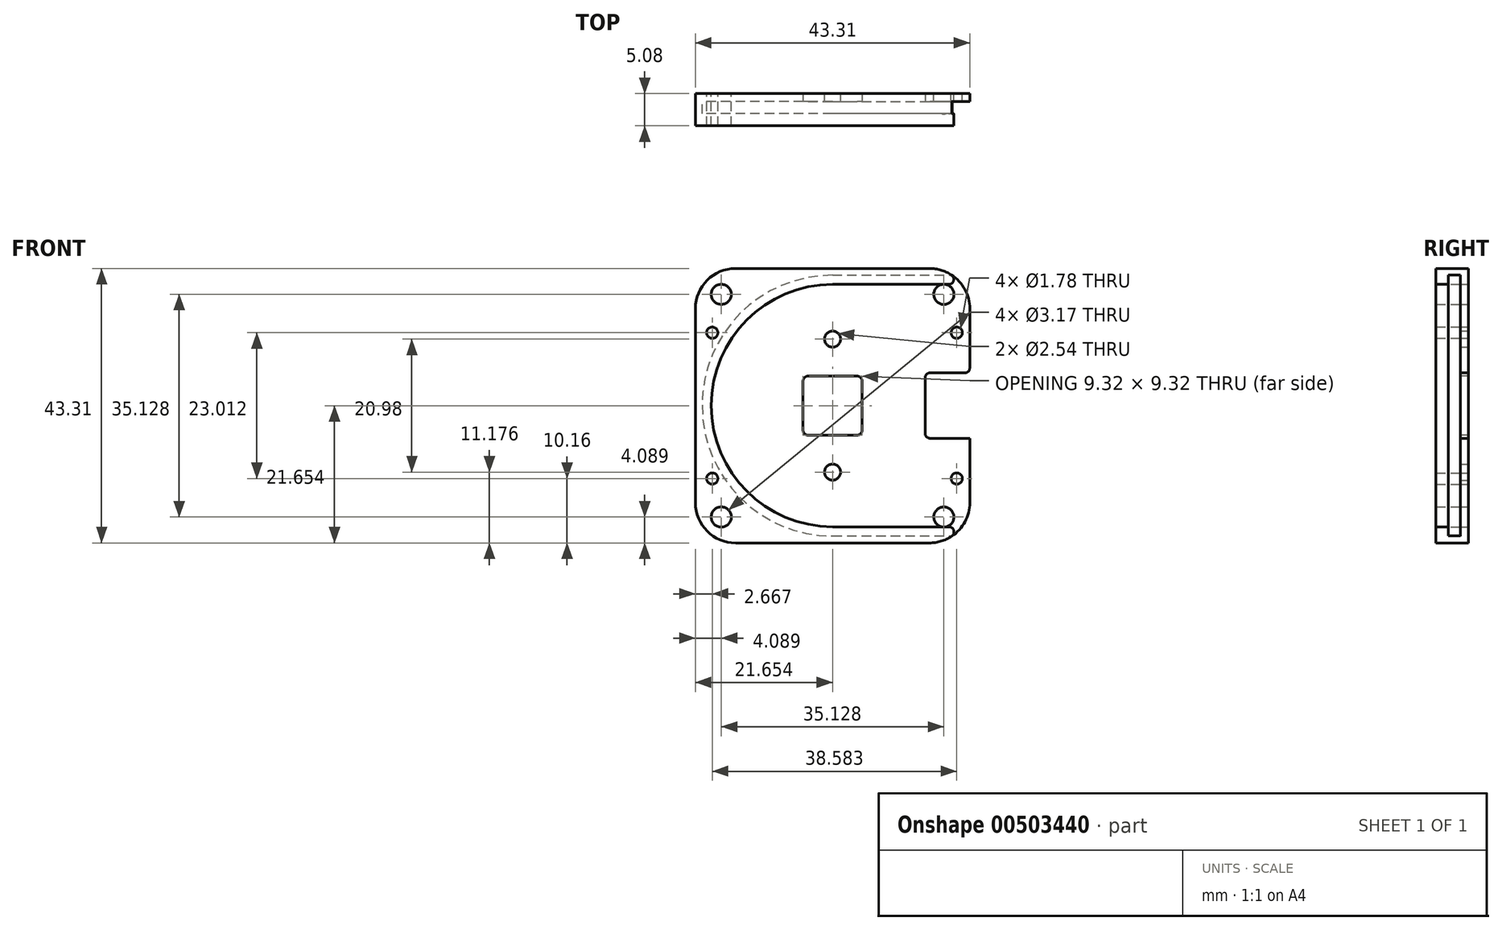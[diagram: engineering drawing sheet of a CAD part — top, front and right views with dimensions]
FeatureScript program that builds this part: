
annotation { "Feature Type Name" : "Feature", "Feature Type Description" : "" }
export const myFeature = defineFeature(function(context is Context, id is Id, definition is map)
    precondition{}
    {
        {
            var Q0;
            Q0=qCreatedBy(makeId("Front.planeOp"),FACE);
            var sketch = newSketch(context, id + "F0", { "sketchPlane" : qUnion([Q0])});
            skLineSegment(sketch, "E0.bottom", {"start": v(0, 0) * mm, "end": v(43.3, 0) * mm});
            skLineSegment(sketch, "E0.top", {"start": v(0, 43.3) * mm, "end": v(43.3, 43.3) * mm});
            skLineSegment(sketch, "E0.left", {"start": v(0, 0) * mm, "end": v(0, 43.3) * mm});
            skLineSegment(sketch, "E0.right", {"start": v(43.3, 0) * mm, "end": v(43.3, 43.3) * mm});
            skSolve(sketch);
        }
        {
            var Q0;
            Q0=makeQuery(id+"F0.imprint","IMPRINT",FACE,{"disambiguationData":[TD([[makeQuery(id+"F0.imprint","IMPRINT",EDGE,{"derivedFrom":sQuery(id+"F0.wireOp",EDGE,"E0.bottom")}),1.0]])]});
            extrude(context, id + "F1", {"entities" : qUnion([Q0]), "depth" : 1.27 * mm});
        }
        {
            var Q0;
            Q0=qCreatedBy(makeId("Front.planeOp"),FACE);
            var sketch = newSketch(context, id + "F2", { "sketchPlane" : qUnion([Q0])});
            skLineSegment(sketch, "E1", {"start": v(0, 43.3) * mm, "end": v(43.3, 43.3) * mm});
            skLineSegment(sketch, "E2", {"start": v(43.3, 43.3) * mm, "end": v(43.3, 42.24) * mm});
            skLineSegment(sketch, "E3", {"start": v(43.3, 42.24) * mm, "end": v(21.64, 42.24) * mm});
            skLineSegment(sketch, "E4", {"start": v(0, 0) * mm, "end": v(43.3, 0) * mm});
            skLineSegment(sketch, "E5", {"start": v(43.3, 0) * mm, "end": v(43.3, 1.1) * mm});
            skLineSegment(sketch, "E6", {"start": v(43.3, 1.1) * mm, "end": v(21.64, 1.1) * mm});
            skArc(sketch, "E7", {"start": v(21.64, 42.24) * mm, "mid": v(1.07, 21.67) * mm, "end": v(21.64, 1.1) * mm});
            skLineSegment(sketch, "E8", {"start": v(0, 43.3) * mm, "end": v(0, 0) * mm});
            skSolve(sketch);
        }
        {
            var Q0;
            Q0 = qSketchRegion(id + "F2", true);
            extrude(context, id + "F3", {"entities" : qUnion([Q0]), "operationType" : NewBodyOperationType.ADD, "depth" : 3.17 * mm});
        }
        {
            var Q0;
            Q0=makeQuery(id+"F3.opExtrude","CAP_FACE",FACE,{"disambiguationData":[OSD([sQuery(id+"F2.wireOp",EDGE,"E1"),sQuery(id+"F2.wireOp",EDGE,"E2"),sQuery(id+"F2.wireOp",EDGE,"E3"),sQuery(id+"F2.wireOp",EDGE,"E4"),sQuery(id+"F2.wireOp",EDGE,"E5"),sQuery(id+"F2.wireOp",EDGE,"E6"),sQuery(id+"F2.wireOp",EDGE,"E7"),sQuery(id+"F2.wireOp",EDGE,"E8")])],"isStart":false});
            var sketch = newSketch(context, id + "F4", { "sketchPlane" : qUnion([Q0])});
            skLineSegment(sketch, "E9", {"start": v(0, 43.3) * mm, "end": v(43.3, 43.3) * mm});
            skLineSegment(sketch, "E10", {"start": v(0, 43.3) * mm, "end": v(0, 0) * mm});
            skLineSegment(sketch, "E11", {"start": v(0, 0) * mm, "end": v(43.3, 0) * mm});
            skLineSegment(sketch, "E12", {"start": v(43.3, 0) * mm, "end": v(43.3, 2.54) * mm});
            skLineSegment(sketch, "E13", {"start": v(43.3, 2.54) * mm, "end": v(21.64, 2.54) * mm});
            skLineSegment(sketch, "E14", {"start": v(43.3, 43.3) * mm, "end": v(43.3, 40.8) * mm});
            skLineSegment(sketch, "E15", {"start": v(43.3, 40.8) * mm, "end": v(21.64, 40.8) * mm});
            skArc(sketch, "E16", {"start": v(21.64, 40.8) * mm, "mid": v(2.51, 21.67) * mm, "end": v(21.64, 2.54) * mm});
            skSolve(sketch);
        }
        {
            var Q0;
            Q0 = qSketchRegion(id + "F4", true);
            extrude(context, id + "F5", {"entities" : qUnion([Q0]), "operationType" : NewBodyOperationType.ADD, "depth" : 1.9 * mm, "offsetDistance" : 25.4 * mm});
        }
        {
            var Q0;
            Q0=makeQuery(id+"F1.opExtrude","CAP_FACE",FACE,{"disambiguationData":[OSD([sQuery(id+"F0.wireOp",EDGE,"E0.bottom"),sQuery(id+"F0.wireOp",EDGE,"E0.top"),sQuery(id+"F0.wireOp",EDGE,"E0.left"),sQuery(id+"F0.wireOp",EDGE,"E0.right")])],"isStart":true});
            var sketch = newSketch(context, id + "F6", { "sketchPlane" : qUnion([Q0])});
            skCircle(sketch, "E17", {"center": v(-41.25, 33.17) * mm, "radius": 0.89 * mm});
            skCircle(sketch, "E18", {"center": v(-2.67, 33.17) * mm, "radius": 0.89 * mm});
            skCircle(sketch, "E19", {"center": v(-41.25, 10.16) * mm, "radius": 0.89 * mm});
            skCircle(sketch, "E20", {"center": v(-2.67, 10.16) * mm, "radius": 0.89 * mm});
            skSolve(sketch);
        }
        {
            var Q0;
            Q0 = qSketchRegion(id + "F6", true);
            extrude(context, id + "F7", {"entities" : qUnion([Q0]), "operationType" : NewBodyOperationType.REMOVE, "endBound" : BoundingType.UP_TO_NEXT, "oppositeDirection" : true, "depth" : 25.4 * mm});
        }
        {
            var Q0;
            Q0=makeQuery(id+"F1.opExtrude","CAP_FACE",FACE,{"disambiguationData":[OSD([sQuery(id+"F0.wireOp",EDGE,"E0.bottom"),sQuery(id+"F0.wireOp",EDGE,"E0.top"),sQuery(id+"F0.wireOp",EDGE,"E0.left"),sQuery(id+"F0.wireOp",EDGE,"E0.right")])],"isStart":false});
            var sketch = newSketch(context, id + "F8", { "sketchPlane" : qUnion([Q0])});
            skLineSegment(sketch, "E21.bottom", {"start": v(17, 26.31) * mm, "end": v(26.31, 26.31) * mm});
            skLineSegment(sketch, "E21.top", {"start": v(17, 17) * mm, "end": v(26.31, 17) * mm});
            skLineSegment(sketch, "E21.left", {"start": v(17, 26.31) * mm, "end": v(17, 17) * mm});
            skLineSegment(sketch, "E21.right", {"start": v(26.31, 26.31) * mm, "end": v(26.31, 17) * mm});
            skLineSegment(sketch, "E22", {"start": v(43.3, 26.82) * mm, "end": v(36.25, 26.82) * mm});
            skLineSegment(sketch, "E23", {"start": v(36.25, 26.82) * mm, "end": v(36.25, 16.51) * mm});
            skLineSegment(sketch, "E24", {"start": v(36.25, 16.51) * mm, "end": v(43.3, 16.51) * mm});
            skLineSegment(sketch, "E25", {"start": v(43.3, 16.51) * mm, "end": v(43.3, 26.82) * mm});
            skSolve(sketch);
        }
        {
            var Q0;
            Q0=makeQuery(id+"F1.opExtrude","CAP_FACE",FACE,{"disambiguationData":[OSD([sQuery(id+"F0.wireOp",EDGE,"E0.bottom"),sQuery(id+"F0.wireOp",EDGE,"E0.top"),sQuery(id+"F0.wireOp",EDGE,"E0.left"),sQuery(id+"F0.wireOp",EDGE,"E0.right")])],"isStart":true});
            var sketch = newSketch(context, id + "F9", { "sketchPlane" : qUnion([Q0])});
            skPoint(sketch, "E26", {"position": v(-4.09, 39.22) * mm});
            skPoint(sketch, "E27", {"position": v(-39.22, 39.22) * mm});
            skPoint(sketch, "E28", {"position": v(-39.22, 4.09) * mm});
            skPoint(sketch, "E29", {"position": v(-4.09, 4.09) * mm});
            skSolve(sketch);
        }
        {
            var Q0;
            Q0 = qSketchRegion(id + "F8", true);
            extrude(context, id + "F10", {"entities" : qUnion([Q0]), "operationType" : NewBodyOperationType.REMOVE, "endBound" : BoundingType.UP_TO_NEXT, "oppositeDirection" : true, "depth" : 25.4 * mm});
        }
        {
            var Q0;
            Q0=sQuery(id+"F9.wireOp",VERTEX,"E26");
            var Q1;
            Q1=sQuery(id+"F9.wireOp",VERTEX,"E29");
            var Q2;
            Q2=makeQuery(id+"F1.opExtrude","SWEPT_BODY",BODY,{"disambiguationData":[OSD([sQuery(id+"F0.wireOp",EDGE,"E0.bottom"),sQuery(id+"F0.wireOp",EDGE,"E0.top"),sQuery(id+"F0.wireOp",EDGE,"E0.left"),sQuery(id+"F0.wireOp",EDGE,"E0.right")])]});
            hole(context, id + "F11", {"style" : HoleStyle.SIMPLE, "endStyle" : HoleEndStyle.THROUGH, "holeDiameter" : 3.17 * mm, "isTappedThrough" : true, "tappedDepth" : 12.7 * mm, "tapClearance" : 3, "locations" : qUnion([Q0, Q1]), "scope" : qUnion([Q2])});
        }
        {
            var Q0;
            Q0=makeQuery(id+"F1.opExtrude","CAP_FACE",FACE,{"disambiguationData":[OSD([sQuery(id+"F0.wireOp",EDGE,"E0.bottom"),sQuery(id+"F0.wireOp",EDGE,"E0.top"),sQuery(id+"F0.wireOp",EDGE,"E0.left"),sQuery(id+"F0.wireOp",EDGE,"E0.right")])],"isStart":true});
            var sketch = newSketch(context, id + "F12", { "sketchPlane" : qUnion([Q0])});
            skLineSegment(sketch, "E30", {"start": v(-39.22, 39.22) * mm, "end": v(-4.09, 39.22) * mm, "construction": true});
            skLineSegment(sketch, "E31", {"start": v(-4.09, 39.22) * mm, "end": v(-4.09, 4.09) * mm, "construction": true});
            skLineSegment(sketch, "E32", {"start": v(-4.09, 4.09) * mm, "end": v(-39.22, 4.09) * mm, "construction": true});
            skLineSegment(sketch, "E33", {"start": v(-39.22, 4.09) * mm, "end": v(-39.22, 39.22) * mm, "construction": true});
            skSolve(sketch);
        }
        {
            var Q0;
            Q0=makeQuery(id+"F1.opExtrude","CAP_FACE",FACE,{"disambiguationData":[OSD([sQuery(id+"F0.wireOp",EDGE,"E0.bottom"),sQuery(id+"F0.wireOp",EDGE,"E0.top"),sQuery(id+"F0.wireOp",EDGE,"E0.left"),sQuery(id+"F0.wireOp",EDGE,"E0.right")])],"isStart":true});
            var sketch = newSketch(context, id + "F13", { "sketchPlane" : qUnion([Q0])});
            skLineSegment(sketch, "E34", {"start": v(-21.65, 32.16) * mm, "end": v(-21.65, 11.18) * mm});
            skPoint(sketch, "E34.startSnap0", {"position": v(-21.65, 26.31) * mm});
            skPoint(sketch, "E34.endSnap0", {"position": v(-21.65, 26.31) * mm});
            skSolve(sketch);
        }
        {
            var Q0;
            Q0=sQuery(id+"F13.wireOp",VERTEX,"E34.start");
            var Q1;
            Q1=sQuery(id+"F13.wireOp",VERTEX,"E34.end");
            var Q2;
            Q2=makeQuery(id+"F1.opExtrude","SWEPT_BODY",BODY,{"disambiguationData":[OSD([sQuery(id+"F0.wireOp",EDGE,"E0.bottom"),sQuery(id+"F0.wireOp",EDGE,"E0.top"),sQuery(id+"F0.wireOp",EDGE,"E0.left"),sQuery(id+"F0.wireOp",EDGE,"E0.right")])]});
            hole(context, id + "F14", {"style" : HoleStyle.SIMPLE, "endStyle" : HoleEndStyle.THROUGH, "holeDiameter" : 2.54 * mm, "isTappedThrough" : true, "tappedDepth" : 12.7 * mm, "tapClearance" : 3, "locations" : qUnion([Q0, Q1]), "scope" : qUnion([Q2])});
        }
        {
            var Q0;
            Q0=makeQuery(id+"F5.boolean.opBoolean","MERGE",EDGE,{"derivedFrom":[makeQuery(id+"F3.boolean.opBoolean","MERGE",EDGE,{"derivedFrom":[makeQuery(id+"F1.opExtrude","SWEPT_EDGE",EDGE,{"disambiguationData":[OSD([sQuery(id+"F0.wireOp",EDGE,"E0.top"),sQuery(id+"F0.wireOp",EDGE,"E0.left")])]}),makeQuery(id+"F3.opExtrude","SWEPT_EDGE",EDGE,{"disambiguationData":[OSD([sQuery(id+"F2.wireOp",EDGE,"E1"),sQuery(id+"F2.wireOp",EDGE,"E8")])]})]}),makeQuery(id+"F5.opExtrude","SWEPT_EDGE",EDGE,{"disambiguationData":[OSD([sQuery(id+"F4.wireOp",EDGE,"E9"),sQuery(id+"F4.wireOp",EDGE,"E10")])]})]});
            var Q1;
            Q1=makeQuery(id+"F5.boolean.opBoolean","MERGE",EDGE,{"derivedFrom":[makeQuery(id+"F3.boolean.opBoolean","MERGE",EDGE,{"derivedFrom":[makeQuery(id+"F1.opExtrude","SWEPT_EDGE",EDGE,{"disambiguationData":[OSD([sQuery(id+"F0.wireOp",EDGE,"E0.top"),sQuery(id+"F0.wireOp",EDGE,"E0.right")])]}),makeQuery(id+"F3.opExtrude","SWEPT_EDGE",EDGE,{"disambiguationData":[OSD([sQuery(id+"F2.wireOp",EDGE,"E1"),sQuery(id+"F2.wireOp",EDGE,"E2")])]})]}),makeQuery(id+"F5.opExtrude","SWEPT_EDGE",EDGE,{"disambiguationData":[OSD([sQuery(id+"F4.wireOp",EDGE,"E9"),sQuery(id+"F4.wireOp",EDGE,"E14")])]})]});
            var Q2;
            Q2=makeQuery(id+"F5.boolean.opBoolean","MERGE",EDGE,{"derivedFrom":[makeQuery(id+"F3.boolean.opBoolean","MERGE",EDGE,{"derivedFrom":[makeQuery(id+"F1.opExtrude","SWEPT_EDGE",EDGE,{"disambiguationData":[OSD([sQuery(id+"F0.wireOp",EDGE,"E0.bottom"),sQuery(id+"F0.wireOp",EDGE,"E0.right")])]}),makeQuery(id+"F3.opExtrude","SWEPT_EDGE",EDGE,{"disambiguationData":[OSD([sQuery(id+"F2.wireOp",EDGE,"E4"),sQuery(id+"F2.wireOp",EDGE,"E5")])]})]}),makeQuery(id+"F5.opExtrude","SWEPT_EDGE",EDGE,{"disambiguationData":[OSD([sQuery(id+"F4.wireOp",EDGE,"E11"),sQuery(id+"F4.wireOp",EDGE,"E12")])]})]});
            var Q3;
            Q3=makeQuery(id+"F5.boolean.opBoolean","MERGE",EDGE,{"derivedFrom":[makeQuery(id+"F3.boolean.opBoolean","MERGE",EDGE,{"derivedFrom":[makeQuery(id+"F1.opExtrude","SWEPT_EDGE",EDGE,{"disambiguationData":[OSD([sQuery(id+"F0.wireOp",EDGE,"E0.bottom"),sQuery(id+"F0.wireOp",EDGE,"E0.left")])]}),makeQuery(id+"F3.opExtrude","SWEPT_EDGE",EDGE,{"disambiguationData":[OSD([sQuery(id+"F2.wireOp",EDGE,"E4"),sQuery(id+"F2.wireOp",EDGE,"E8")])]})]}),makeQuery(id+"F5.opExtrude","SWEPT_EDGE",EDGE,{"disambiguationData":[OSD([sQuery(id+"F4.wireOp",EDGE,"E10"),sQuery(id+"F4.wireOp",EDGE,"E11")])]})]});
            fillet(context, id + "F15", {"entities" : qUnion([Q0, Q1, Q2, Q3]), "radius" : 6.35 * mm, "tangentPropagation" : true, "allowEdgeOverflow" : false});
        }
        {
            var Q0;
            {var subQ1=sQuery(id+"F4.wireOp",EDGE,"E15");var subQ2=sQuery(id+"F4.wireOp",EDGE,"E14");var subQ7=sQuery(id+"F4.wireOp",EDGE,"E9");var subQ8=sQuery(id+"F2.wireOp",EDGE,"E2");var subQ9=sQuery(id+"F0.wireOp",EDGE,"E0.right");Q0=makeQuery(id+"F15.opFillet","BLEND_EDGE",EDGE,{"blendedFrom":[makeQuery(id+"F5.boolean.opBoolean","MERGE",EDGE,{"derivedFrom":[makeQuery(id+"F3.boolean.opBoolean","MERGE",EDGE,{"derivedFrom":[makeQuery(id+"F1.opExtrude","SWEPT_EDGE",EDGE,{"disambiguationData":[OSD([sQuery(id+"F0.wireOp",EDGE,"E0.top"),subQ9])]}),makeQuery(id+"F3.opExtrude","SWEPT_EDGE",EDGE,{"disambiguationData":[OSD([sQuery(id+"F2.wireOp",EDGE,"E1"),subQ8])]})]}),makeQuery(id+"F5.opExtrude","SWEPT_EDGE",EDGE,{"disambiguationData":[OSD([subQ7,subQ2])]})]}),makeQuery(id+"FAVqUnOOAbN4NIG_1.hole-0.boolean.opBoolean","SPLIT",FACE,{"disambiguationData":[TD([makeQuery(id+"F1.opExtrude","SWEPT_FACE",FACE,{"disambiguationData":[OSD([subQ9])]})])],"derivedFrom":makeQuery(id+"F5.opExtrude","SWEPT_FACE",FACE,{"disambiguationData":[OSD([subQ1])]})})],"blendedInto":[makeQuery(id+"FAVqUnOOAbN4NIG_1.hole-0.boolean.opBoolean","SPLIT",FACE,{"disambiguationData":[TD([makeQuery(id+"F1.opExtrude","SWEPT_FACE",FACE,{"disambiguationData":[OSD([subQ9])]})])],"derivedFrom":makeQuery(id+"F5.opExtrude","SWEPT_FACE",FACE,{"disambiguationData":[OSD([subQ1])]})})]});}
            var Q1;
            {var subQ3=sQuery(id+"F4.wireOp",EDGE,"E13");var subQ4=sQuery(id+"F4.wireOp",EDGE,"E12");var subQ5=sQuery(id+"F4.wireOp",EDGE,"E11");var subQ8=sQuery(id+"F2.wireOp",EDGE,"E5");var subQ9=sQuery(id+"F0.wireOp",EDGE,"E0.right");Q1=makeQuery(id+"F15.opFillet","BLEND_EDGE",EDGE,{"blendedFrom":[makeQuery(id+"F5.boolean.opBoolean","MERGE",EDGE,{"derivedFrom":[makeQuery(id+"F3.boolean.opBoolean","MERGE",EDGE,{"derivedFrom":[makeQuery(id+"F1.opExtrude","SWEPT_EDGE",EDGE,{"disambiguationData":[OSD([sQuery(id+"F0.wireOp",EDGE,"E0.bottom"),subQ9])]}),makeQuery(id+"F3.opExtrude","SWEPT_EDGE",EDGE,{"disambiguationData":[OSD([sQuery(id+"F2.wireOp",EDGE,"E4"),subQ8])]})]}),makeQuery(id+"F5.opExtrude","SWEPT_EDGE",EDGE,{"disambiguationData":[OSD([subQ5,subQ4])]})]}),makeQuery(id+"FAVqUnOOAbN4NIG_1.hole-3.boolean.opBoolean","SPLIT",FACE,{"disambiguationData":[TD([makeQuery(id+"F1.opExtrude","SWEPT_FACE",FACE,{"disambiguationData":[OSD([subQ9])]})])],"derivedFrom":makeQuery(id+"F5.opExtrude","SWEPT_FACE",FACE,{"disambiguationData":[OSD([subQ3])]})})],"blendedInto":[makeQuery(id+"FAVqUnOOAbN4NIG_1.hole-3.boolean.opBoolean","SPLIT",FACE,{"disambiguationData":[TD([makeQuery(id+"F1.opExtrude","SWEPT_FACE",FACE,{"disambiguationData":[OSD([subQ9])]})])],"derivedFrom":makeQuery(id+"F5.opExtrude","SWEPT_FACE",FACE,{"disambiguationData":[OSD([subQ3])]})})]});}
            fillet(context, id + "F16", {"entities" : qUnion([Q0, Q1]), "radius" : 0.81 * mm, "tangentPropagation" : true, "allowEdgeOverflow" : false});
        }
        {
            var Q0;
            Q0=makeQuery(id+"F10.boolean.opBoolean","COPY",EDGE,{"derivedFrom":makeQuery(id+"F10.opExtrude","SWEPT_EDGE",EDGE,{"disambiguationData":[OSD([sQuery(id+"F0.wireOp",EDGE,"E0.right"),sQuery(id+"F8.wireOp",EDGE,"E22"),sQuery(id+"F8.wireOp",EDGE,"E25")])]})});
            var Q1;
            Q1=makeQuery(id+"F10.boolean.opBoolean","COPY",EDGE,{"derivedFrom":makeQuery(id+"F10.opExtrude","SWEPT_EDGE",EDGE,{"disambiguationData":[OSD([sQuery(id+"F8.wireOp",EDGE,"E22"),sQuery(id+"F8.wireOp",EDGE,"E23")])]})});
            var Q2;
            Q2=makeQuery(id+"F10.boolean.opBoolean","COPY",EDGE,{"derivedFrom":makeQuery(id+"F10.opExtrude","SWEPT_EDGE",EDGE,{"disambiguationData":[OSD([sQuery(id+"F8.wireOp",EDGE,"E21.bottom"),sQuery(id+"F8.wireOp",EDGE,"E21.left")])]})});
            var Q3;
            Q3=makeQuery(id+"F10.boolean.opBoolean","COPY",EDGE,{"derivedFrom":makeQuery(id+"F10.opExtrude","SWEPT_EDGE",EDGE,{"disambiguationData":[OSD([sQuery(id+"F8.wireOp",EDGE,"E21.top"),sQuery(id+"F8.wireOp",EDGE,"E21.left")])]})});
            var Q4;
            Q4=makeQuery(id+"F10.boolean.opBoolean","COPY",EDGE,{"derivedFrom":makeQuery(id+"F10.opExtrude","SWEPT_EDGE",EDGE,{"disambiguationData":[OSD([sQuery(id+"F8.wireOp",EDGE,"E21.top"),sQuery(id+"F8.wireOp",EDGE,"E21.right")])]})});
            var Q5;
            Q5=makeQuery(id+"F10.boolean.opBoolean","COPY",EDGE,{"derivedFrom":makeQuery(id+"F10.opExtrude","SWEPT_EDGE",EDGE,{"disambiguationData":[OSD([sQuery(id+"F0.wireOp",EDGE,"E0.right"),sQuery(id+"F8.wireOp",EDGE,"E24"),sQuery(id+"F8.wireOp",EDGE,"E25")])]})});
            var Q6;
            Q6=makeQuery(id+"F10.boolean.opBoolean","COPY",EDGE,{"derivedFrom":makeQuery(id+"F10.opExtrude","SWEPT_EDGE",EDGE,{"disambiguationData":[OSD([sQuery(id+"F8.wireOp",EDGE,"E23"),sQuery(id+"F8.wireOp",EDGE,"E24")])]})});
            var Q7;
            Q7=makeQuery(id+"F10.boolean.opBoolean","COPY",EDGE,{"derivedFrom":makeQuery(id+"F10.opExtrude","SWEPT_EDGE",EDGE,{"disambiguationData":[OSD([sQuery(id+"F8.wireOp",EDGE,"E21.bottom"),sQuery(id+"F8.wireOp",EDGE,"E21.right")])]})});
            fillet(context, id + "F17", {"entities" : qUnion([Q0, Q1, Q2, Q3, Q4, Q5, Q6, Q7]), "radius" : 0.79 * mm, "tangentPropagation" : true, "allowEdgeOverflow" : false});
        }
        {
            var Q0;
            Q0=sQuery(id+"F12.wireOp",VERTEX,"E33.start");
            var Q1;
            Q1=sQuery(id+"F12.wireOp",VERTEX,"E33.end");
            var Q2;
            Q2=makeQuery(id+"F1.opExtrude","SWEPT_BODY",BODY,{"disambiguationData":[OSD([sQuery(id+"F0.wireOp",EDGE,"E0.bottom"),sQuery(id+"F0.wireOp",EDGE,"E0.top"),sQuery(id+"F0.wireOp",EDGE,"E0.left"),sQuery(id+"F0.wireOp",EDGE,"E0.right")])]});
            hole(context, id + "F18", {"style" : HoleStyle.SIMPLE, "endStyle" : HoleEndStyle.BLIND, "holeDiameter" : 3.17 * mm, "holeDepth" : 3.17 * mm, "isTappedThrough" : true, "tappedDepth" : 12.7 * mm, "tapClearance" : 3, "locations" : qUnion([Q0, Q1]), "scope" : qUnion([Q2])});
        }
    });
